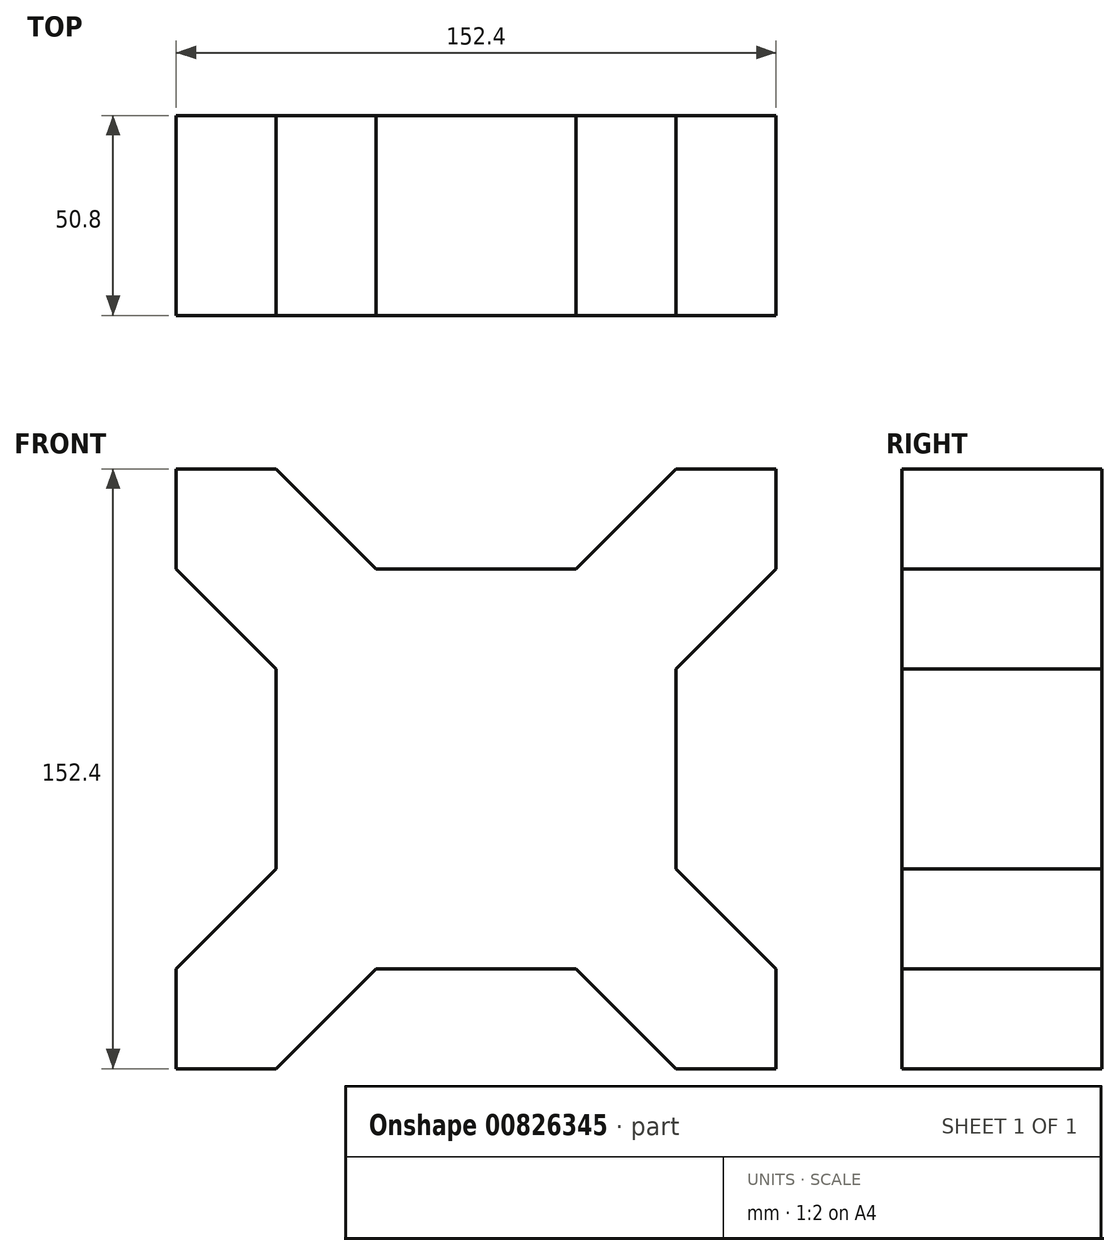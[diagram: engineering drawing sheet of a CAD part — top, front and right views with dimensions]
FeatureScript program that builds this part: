
annotation { "Feature Type Name" : "Feature", "Feature Type Description" : "" }
export const myFeature = defineFeature(function(context is Context, id is Id, definition is map)
    precondition{}
    {
        {
            var Q0;
            Q0=qCreatedBy(makeId("Front.planeOp"),FACE);
            var sketch = newSketch(context, id + "F0", { "sketchPlane" : qUnion([Q0])});
            skLineSegment(sketch, "E0", {"start": v(0, 0) * mm, "end": v(-50.8, 0) * mm, "construction": true});
            skLineSegment(sketch, "E1", {"start": v(0, 50.8) * mm, "end": v(-50.8, 50.8) * mm, "construction": true});
            skLineSegment(sketch, "E2.bottom", {"start": v(-25.4, 50.8) * mm, "end": v(0, 50.8) * mm});
            skLineSegment(sketch, "E2.top", {"start": v(-25.4, -50.8) * mm, "end": v(0, -50.8) * mm});
            skLineSegment(sketch, "E2.left", {"start": v(-50.8, 25.4) * mm, "end": v(-50.8, -25.4) * mm});
            skLineSegment(sketch, "E3.top", {"start": v(-50.8, 76.2) * mm, "end": v(-76.2, 76.2) * mm});
            skLineSegment(sketch, "E3.right", {"start": v(-76.2, 50.8) * mm, "end": v(-76.2, 76.2) * mm});
            skLineSegment(sketch, "E4.top", {"start": v(-50.8, -76.2) * mm, "end": v(-76.2, -76.2) * mm});
            skLineSegment(sketch, "E4.right", {"start": v(-76.2, -50.8) * mm, "end": v(-76.2, -76.2) * mm});
            skLineSegment(sketch, "E5", {"start": v(-50.8, 25.4) * mm, "end": v(-76.2, 50.8) * mm});
            skPoint(sketch, "E5.startSnap0", {"position": v(0, 25.4) * mm});
            skLineSegment(sketch, "E6", {"start": v(-50.8, 76.2) * mm, "end": v(-25.4, 50.8) * mm});
            skPoint(sketch, "E7.startSnap1", {"position": v(-50.8, -63.5) * mm});
            skLineSegment(sketch, "E8", {"start": v(-50.8, -76.2) * mm, "end": v(-25.4, -50.8) * mm});
            skPoint(sketch, "E8.endSnap0", {"position": v(-25.4, 0) * mm});
            skLineSegment(sketch, "E9", {"start": v(-76.2, -50.8) * mm, "end": v(-50.8, -25.4) * mm});
            skLineSegment(sketch, "E10", {"start": v(0, 76.2) * mm, "end": v(0, -76.2) * mm, "construction": true});
            skLineSegment(sketch, "E11.MirrorCS", {"start": v(50.8, 76.2) * mm, "end": v(25.4, 50.8) * mm});
            skLineSegment(sketch, "E12.MirrorCS", {"start": v(25.4, 50.8) * mm, "end": v(0, 50.8) * mm});
            skLineSegment(sketch, "E13.MirrorCS", {"start": v(50.8, 76.2) * mm, "end": v(76.2, 76.2) * mm});
            skLineSegment(sketch, "E14.MirrorCS", {"start": v(76.2, 50.8) * mm, "end": v(76.2, 76.2) * mm});
            skLineSegment(sketch, "E15.MirrorCS", {"start": v(50.8, 25.4) * mm, "end": v(76.2, 50.8) * mm});
            skLineSegment(sketch, "E16.MirrorCS", {"start": v(50.8, 25.4) * mm, "end": v(50.8, -25.4) * mm});
            skLineSegment(sketch, "E17.MirrorCS", {"start": v(76.2, -50.8) * mm, "end": v(50.8, -25.4) * mm});
            skLineSegment(sketch, "E18.MirrorCS", {"start": v(76.2, -50.8) * mm, "end": v(76.2, -76.2) * mm});
            skLineSegment(sketch, "E19.MirrorCS", {"start": v(50.8, -76.2) * mm, "end": v(76.2, -76.2) * mm});
            skLineSegment(sketch, "E20.MirrorCS", {"start": v(50.8, -76.2) * mm, "end": v(25.4, -50.8) * mm});
            skLineSegment(sketch, "E21.MirrorCS", {"start": v(25.4, -50.8) * mm, "end": v(0, -50.8) * mm});
            skPoint(sketch, "E22.orphan", {"position": v(50.8, 50.8) * mm});
            skPoint(sketch, "E23.MirrorCS.end.orphan", {"position": v(76.2, 50.8) * mm});
            skPoint(sketch, "E24.orphan", {"position": v(50.8, -50.8) * mm});
            skPoint(sketch, "E25.orphan", {"position": v(-50.8, -50.8) * mm});
            skSolve(sketch);
        }
        {
            var Q0;
            Q0=makeQuery(id+"F0.imprint","IMPRINT",FACE,{"disambiguationData":[TD([[makeQuery(id+"F0.imprint","IMPRINT",EDGE,{"derivedFrom":sQuery(id+"F0.wireOp",EDGE,"E2.bottom")}),-1.0]])]});
            extrude(context, id + "F1", {"entities" : qUnion([Q0]), "depth" : 50.8 * mm, "offsetDistance" : 25.4 * mm});
        }
    });
